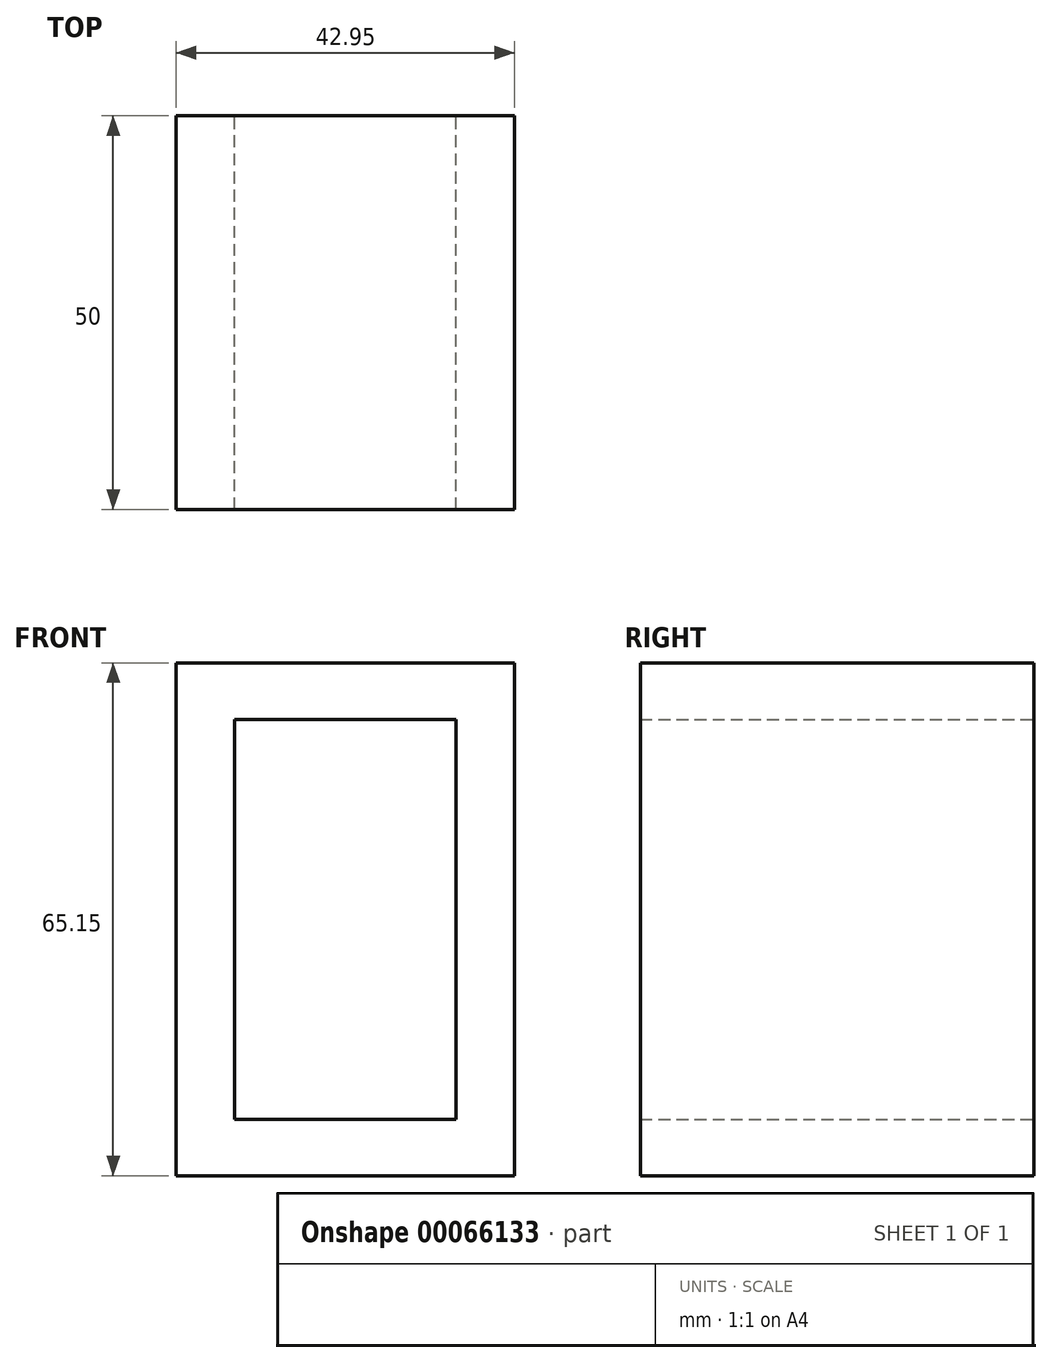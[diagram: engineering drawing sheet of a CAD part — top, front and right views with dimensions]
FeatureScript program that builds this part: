
annotation { "Feature Type Name" : "Feature", "Feature Type Description" : "" }
export const myFeature = defineFeature(function(context is Context, id is Id, definition is map)
    precondition{}
    {
        {
            var Q0;
            Q0=qCreatedBy(makeId("Front.planeOp"),FACE);
            var sketch = newSketch(context, id + "F0", { "sketchPlane" : qUnion([Q0])});
            skLineSegment(sketch, "E0.rect.top", {"start": v(-73.63, 115.44) * mm, "end": v(-49.13, 115.44) * mm});
            skLineSegment(sketch, "E0.rect.left", {"start": v(-73.63, 88.25) * mm, "end": v(-73.63, 115.44) * mm});
            skLineSegment(sketch, "E0.rect.right", {"start": v(-49.13, 88.25) * mm, "end": v(-49.13, 115.44) * mm});
            skLineSegment(sketch, "E1.rect.right", {"start": v(73.8, 62.5) * mm, "end": v(73.8, 75.25) * mm});
            skLineSegment(sketch, "E2.rect.bottom", {"start": v(-14.2, 12.22) * mm, "end": v(-42.33, 12.22) * mm});
            skLineSegment(sketch, "E2.rect.top", {"start": v(-14.2, 63.02) * mm, "end": v(-42.33, 63.02) * mm});
            skLineSegment(sketch, "E2.rect.left", {"start": v(-14.2, 12.22) * mm, "end": v(-14.2, 63.02) * mm});
            skLineSegment(sketch, "E2.rect.right", {"start": v(-42.33, 12.22) * mm, "end": v(-42.33, 63.02) * mm});
            skPoint(sketch, "E2.rect.middle", {"position": v(-28.26, 37.62) * mm});
            skLineSegment(sketch, "E3.rect.bottom", {"start": v(-49.74, 70.2) * mm, "end": v(-6.8, 70.2) * mm});
            skLineSegment(sketch, "E3.rect.top", {"start": v(-49.74, 5.05) * mm, "end": v(-6.8, 5.05) * mm});
            skLineSegment(sketch, "E3.rect.left", {"start": v(-49.74, 70.2) * mm, "end": v(-49.74, 5.05) * mm});
            skLineSegment(sketch, "E3.rect.right", {"start": v(-6.8, 70.2) * mm, "end": v(-6.8, 5.05) * mm});
            skSolve(sketch);
        }
        {
            var Q0;
            Q0=makeQuery(id+"F0.imprint","IMPRINT",FACE,{"disambiguationData":[TD([[makeQuery(id+"F0.imprint","IMPRINT",EDGE,{"derivedFrom":sQuery(id+"F0.wireOp",EDGE,"E2.rect.bottom")}),1.0]])]});
            extrude(context, id + "F1", {"entities" : qUnion([Q0]), "depth" : 50 * mm});
        }
    });
